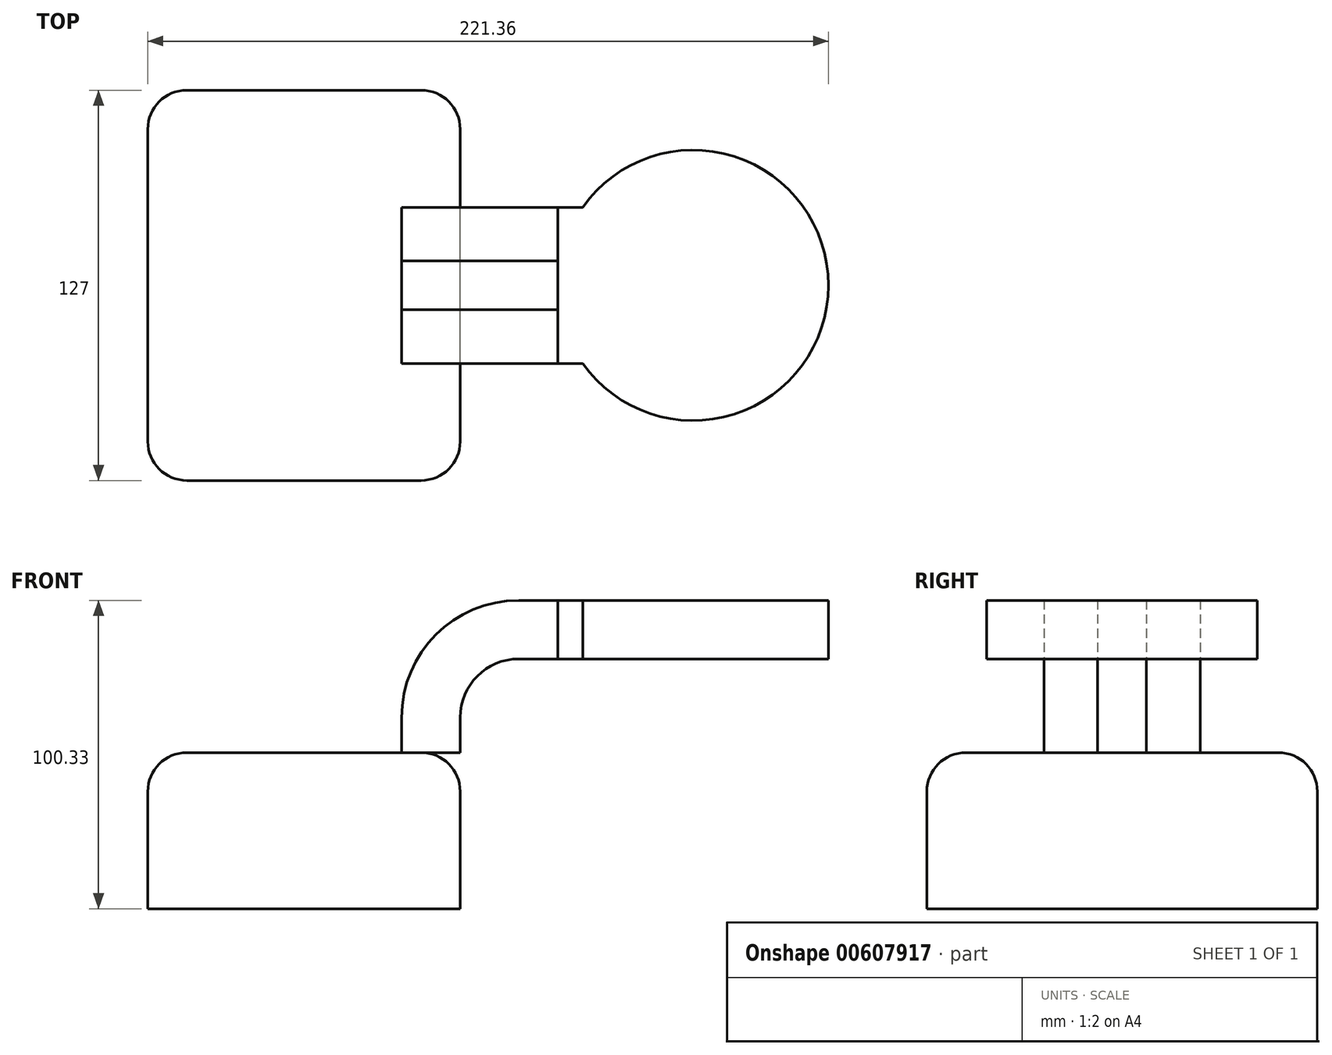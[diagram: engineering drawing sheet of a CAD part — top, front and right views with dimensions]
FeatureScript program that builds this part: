
annotation { "Feature Type Name" : "Feature", "Feature Type Description" : "" }
export const myFeature = defineFeature(function(context is Context, id is Id, definition is map)
    precondition{}
    {
        {
            var Q0;
            Q0=qCreatedBy(makeId("Front.planeOp"),FACE);
            var sketch = newSketch(context, id + "F0", { "sketchPlane" : qUnion([Q0])});
            skLineSegment(sketch, "E0.bottom", {"start": v(-50.8, 25.4) * mm, "end": v(50.8, 25.4) * mm});
            skLineSegment(sketch, "E0.top", {"start": v(-50.8, -25.4) * mm, "end": v(50.8, -25.4) * mm});
            skLineSegment(sketch, "E0.left", {"start": v(-50.8, 25.4) * mm, "end": v(-50.8, -25.4) * mm});
            skLineSegment(sketch, "E0.right", {"start": v(50.8, 25.4) * mm, "end": v(50.8, -25.4) * mm});
            skPoint(sketch, "E0.middle", {"position": v(0, 0) * mm});
            skLineSegment(sketch, "E1.bottom", {"start": v(82.55, 74.93) * mm, "end": v(158.75, 74.93) * mm});
            skLineSegment(sketch, "E1.top", {"start": v(82.55, 44.45) * mm, "end": v(158.75, 44.45) * mm});
            skLineSegment(sketch, "E1.left", {"start": v(82.55, 74.93) * mm, "end": v(82.55, 44.45) * mm});
            skLineSegment(sketch, "E1.right", {"start": v(158.75, 74.93) * mm, "end": v(158.75, 44.45) * mm});
            skPoint(sketch, "E1.middle", {"position": v(120.65, 59.69) * mm});
            skLineSegment(sketch, "E2", {"start": v(50.8, 25.4) * mm, "end": v(50.8, 36.83) * mm});
            skArc(sketch, "E3", {"start": v(50.8, 36.83) * mm, "mid": v(56.38, 50.3) * mm, "end": v(69.85, 55.88) * mm});
            skLineSegment(sketch, "E4", {"start": v(69.85, 55.88) * mm, "end": v(126.55, 55.88) * mm});
            skLineSegment(sketch, "E5.0", {"start": v(69.85, 74.93) * mm, "end": v(126.55, 74.93) * mm});
            skArc(sketch, "E5.1", {"start": v(31.75, 36.83) * mm, "mid": v(42.9, 63.77) * mm, "end": v(69.85, 74.93) * mm});
            skLineSegment(sketch, "E5.2", {"start": v(31.75, 25.4) * mm, "end": v(31.75, 36.83) * mm});
            skFitSpline(sketch, "E6", {"points": [v(-50.8, 25.4) * mm, v(69.85, 74.93) * mm], "startDerivative": vector(73.53, 91.15) * mm, "endDerivative": vector(162.23, -2.09) * mm});
            skLineSegment(sketch, "E7", {"start": v(126.55, 74.93) * mm, "end": v(126.55, 44.45) * mm});
            skSolve(sketch);
        }
        {
            var Q0;
            {var subQ0=sQuery(id+"F0.wireOp",EDGE,"E5.0");var subQ1=sQuery(id+"F0.wireOp",EDGE,"E1.left");var subQ2=makeQuery(id+"F0.imprint","INTERSECT",VERTEX,{"derivedFrom":[subQ1,subQ0]});Q0=makeQuery(id+"F0.imprint","IMPRINT",FACE,{"disambiguationData":[TD([[makeQuery(id+"F0.imprint","IMPRINT",EDGE,{"disambiguationData":[TD([[subQ2,-1.0]])],"derivedFrom":subQ1}),1.0]])]});}
            extrude(context, id + "F1", {"entities" : qUnion([Q0]), "endBound" : BoundingType.SYMMETRIC, "depth" : 50.8 * mm, "offsetDistance" : 25.4 * mm});
        }
        {
            var Q0;
            Q0=makeQuery(id+"F0.imprint","IMPRINT",FACE,{"disambiguationData":[TD([[makeQuery(id+"F0.imprint","IMPRINT",EDGE,{"derivedFrom":sQuery(id+"F0.wireOp",EDGE,"E0.top")}),1.0]])]});
            extrude(context, id + "F2", {"entities" : qUnion([Q0]), "endBound" : BoundingType.SYMMETRIC, "depth" : 127 * mm, "offsetDistance" : 25.4 * mm});
        }
        {
            var Q0;
            Q0=makeQuery(id+"F0.imprint","IMPRINT",FACE,{"disambiguationData":[TD([[makeQuery(id+"F0.imprint","IMPRINT",EDGE,{"derivedFrom":sQuery(id+"F0.wireOp",EDGE,"E5.1")}),1.0]])]});
            extrude(context, id + "F3", {"entities" : qUnion([Q0]), "endBound" : BoundingType.SYMMETRIC, "depth" : 15.88 * mm, "offsetDistance" : 25.4 * mm});
        }
        {
            var Q0;
            {var subQ4=sQuery(id+"F0.wireOp",EDGE,"E1.bottom");Q0=makeQuery(id+"F0.imprint","IMPRINT",FACE,{"disambiguationData":[TD([[makeQuery(id+"F0.imprint","IMPRINT",EDGE,{"derivedFrom":subQ4}),-1.0]])]});}
            var Q1;
            Q1=sQuery(id+"F0.wireOp",EDGE,"E7");
            revolve(context, id + "F4", {"operationType" : NewBodyOperationType.ADD, "entities" : qUnion([Q0]), "axis" : qUnion([Q1]), "revolveType" : RevolveType.FULL});
        }
        {
            var Q0;
            {var subQ1=sQuery(id+"F0.wireOp",EDGE,"E2");Q0=makeQuery(id+"F0.imprint","IMPRINT",FACE,{"disambiguationData":[TD([[makeQuery(id+"F0.imprint","IMPRINT",EDGE,{"derivedFrom":subQ1}),1.0]])]});}
            extrude(context, id + "F5", {"entities" : qUnion([Q0]), "endBound" : BoundingType.SYMMETRIC, "depth" : 50.8 * mm, "offsetDistance" : 25.4 * mm});
        }
        {
            var Q0;
            Q0=makeQuery(id+"F2.opExtrude","CAP_EDGE",EDGE,{"disambiguationData":[OSD([sQuery(id+"F0.wireOp",EDGE,"E0.right")])],"isStart":false});
            var Q1;
            Q1=makeQuery(id+"F2.opExtrude","CAP_EDGE",EDGE,{"disambiguationData":[OSD([sQuery(id+"F0.wireOp",EDGE,"E0.left")])],"isStart":false});
            var Q2;
            Q2=makeQuery(id+"F2.opExtrude","CAP_EDGE",EDGE,{"disambiguationData":[OSD([sQuery(id+"F0.wireOp",EDGE,"E0.left")])],"isStart":true});
            var Q3;
            Q3=makeQuery(id+"F2.opExtrude","CAP_EDGE",EDGE,{"disambiguationData":[OSD([sQuery(id+"F0.wireOp",EDGE,"E0.right")])],"isStart":true});
            fillet(context, id + "F6", {"entities" : qUnion([Q0, Q1, Q2, Q3]), "radius" : 12.7 * mm, "tangentPropagation" : true, "allowEdgeOverflow" : false});
        }
        {
            var Q0;
            Q0=makeQuery(id+"F2.opExtrude","CAP_EDGE",EDGE,{"disambiguationData":[OSD([sQuery(id+"F0.wireOp",EDGE,"E0.bottom")])],"isStart":true});
            var Q1;
            Q1=makeQuery(id+"F2.opExtrude","SWEPT_EDGE",EDGE,{"disambiguationData":[OSD([sQuery(id+"F0.wireOp",EDGE,"E0.bottom"),sQuery(id+"F0.wireOp",EDGE,"E0.left"),sQuery(id+"F0.wireOp",EDGE,"E6")])]});
            var Q2;
            Q2=makeQuery(id+"F2.opExtrude","CAP_EDGE",EDGE,{"disambiguationData":[OSD([sQuery(id+"F0.wireOp",EDGE,"E0.bottom")])],"isStart":false});
            var Q3;
            Q3=makeQuery(id+"F2.opExtrude","SWEPT_EDGE",EDGE,{"disambiguationData":[OSD([sQuery(id+"F0.wireOp",EDGE,"E0.bottom"),sQuery(id+"F0.wireOp",EDGE,"E0.right"),sQuery(id+"F0.wireOp",EDGE,"E2")])]});
            fillet(context, id + "F7", {"entities" : qUnion([Q0, Q1, Q2, Q3]), "radius" : 12.7 * mm, "tangentPropagation" : true, "allowEdgeOverflow" : false});
        }
    });
